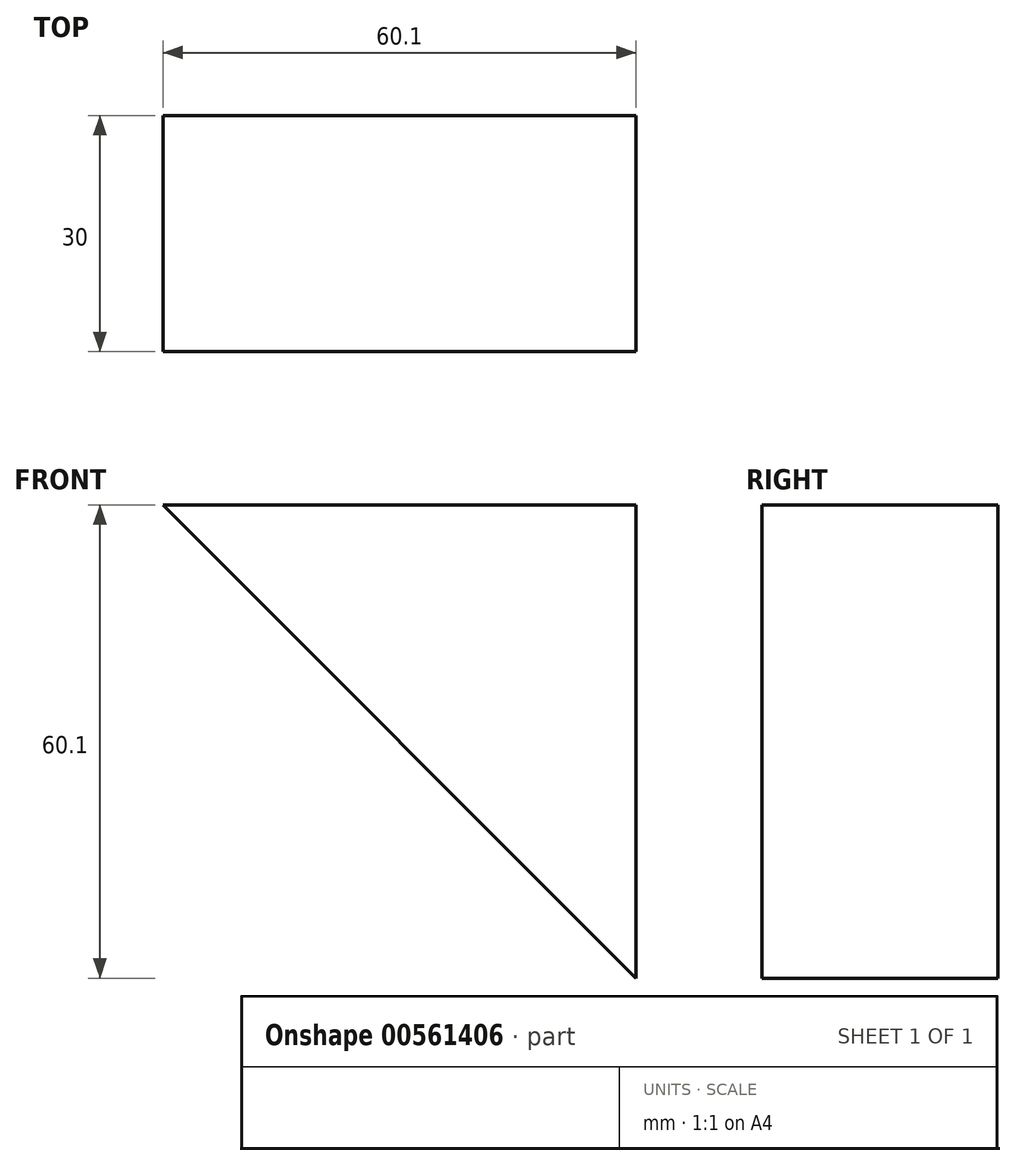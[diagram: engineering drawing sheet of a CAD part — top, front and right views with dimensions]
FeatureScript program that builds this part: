
annotation { "Feature Type Name" : "Feature", "Feature Type Description" : "" }
export const myFeature = defineFeature(function(context is Context, id is Id, definition is map)
    precondition{}
    {
        {
            var Q0;
            Q0=qCreatedBy(makeId("Front.planeOp"),FACE);
            var sketch = newSketch(context, id + "F0", { "sketchPlane" : qUnion([Q0])});
            skPoint(sketch, "E0.end.orphan", {"position": v(0, 15.49) * mm});
            skLineSegment(sketch, "E1", {"start": v(14.98, 79.77) * mm, "end": v(75.08, 79.77) * mm});
            skLineSegment(sketch, "E2", {"start": v(75.08, 79.77) * mm, "end": v(75.08, 19.67) * mm});
            skLineSegment(sketch, "E3", {"start": v(75.08, 19.67) * mm, "end": v(14.98, 79.77) * mm});
            skSolve(sketch);
        }
        {
            var Q0;
            Q0 = qSketchRegion(id + "F0", true);
            extrude(context, id + "F1", {"entities" : qUnion([Q0]), "depth" : 30 * mm, "offsetDistance" : 25 * mm});
        }
    });
